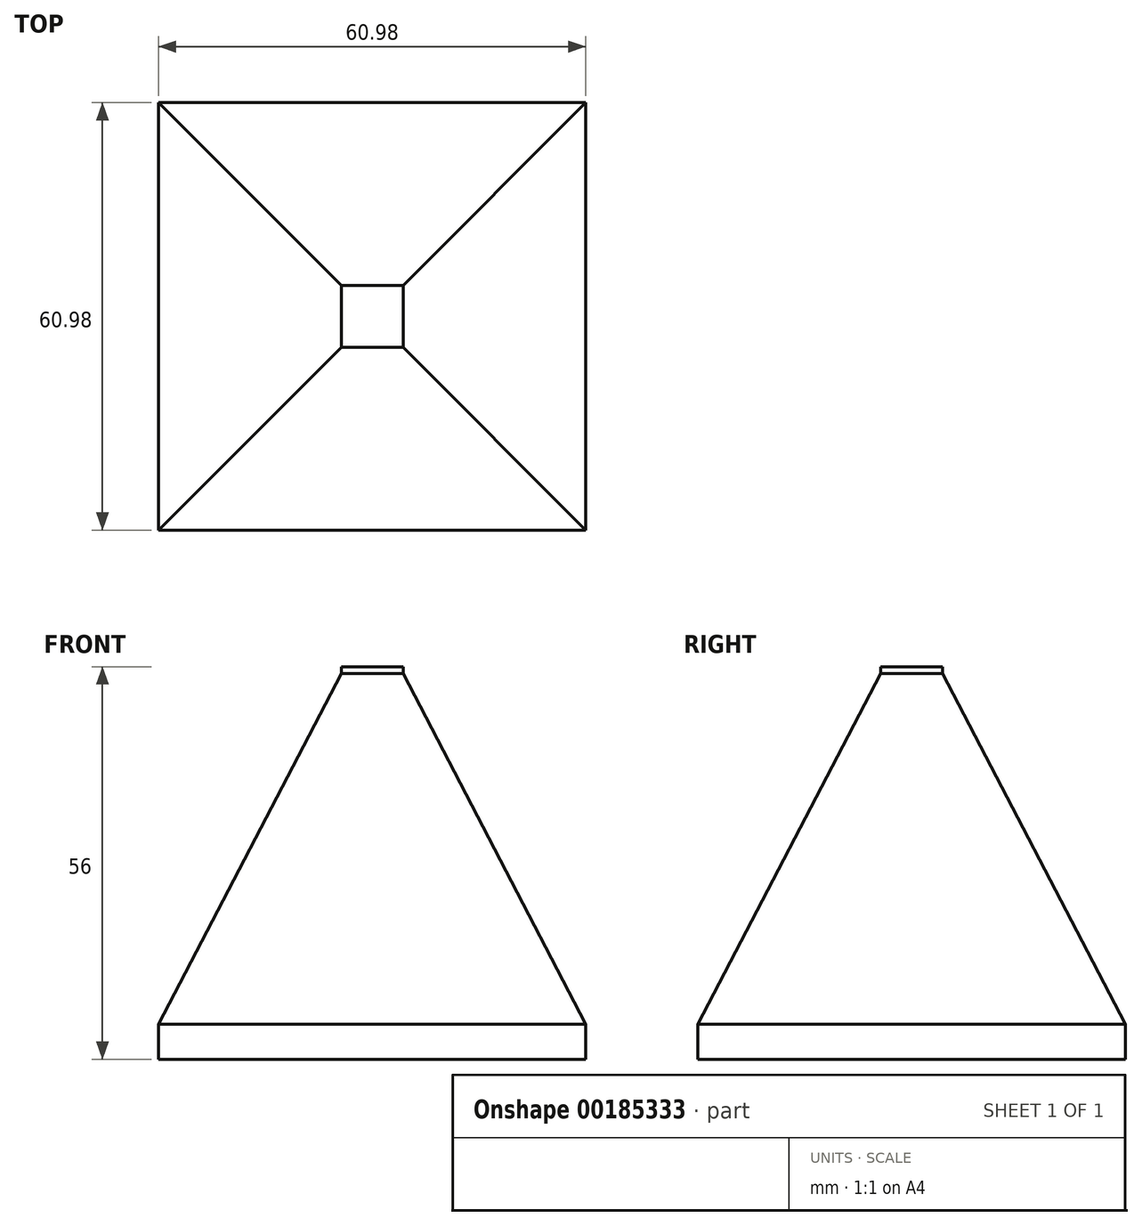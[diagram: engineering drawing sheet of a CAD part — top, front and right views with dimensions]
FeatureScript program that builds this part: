
annotation { "Feature Type Name" : "Feature", "Feature Type Description" : "" }
export const myFeature = defineFeature(function(context is Context, id is Id, definition is map)
    precondition{}
    {
        {
            var Q0;
            Q0=qCreatedBy(makeId("Top.planeOp"),FACE);
            var sketch = newSketch(context, id + "F0", { "sketchPlane" : qUnion([Q0])});
            skLineSegment(sketch, "E0.bottom", {"start": v(30.5, 30.5) * mm, "end": v(-30.5, 30.5) * mm});
            skLineSegment(sketch, "E0.top", {"start": v(30.5, -30.5) * mm, "end": v(-30.5, -30.5) * mm});
            skLineSegment(sketch, "E0.left", {"start": v(30.5, 30.5) * mm, "end": v(30.5, -30.5) * mm});
            skLineSegment(sketch, "E0.right", {"start": v(-30.5, 30.5) * mm, "end": v(-30.5, -30.5) * mm});
            skPoint(sketch, "E0.middle", {"position": v(0, 0) * mm});
            skSolve(sketch);
        }
        {
            var Q0;
            Q0=makeQuery(id+"F0.imprint","IMPRINT",FACE,{"disambiguationData":[TD([[makeQuery(id+"F0.imprint","IMPRINT",EDGE,{"derivedFrom":sQuery(id+"F0.wireOp",EDGE,"E0.bottom")}),1.0]])]});
            extrude(context, id + "F1", {"entities" : qUnion([Q0]), "depth" : 5 * mm});
        }
        {
            var Q0;
            Q0=makeQuery(id+"F1.opExtrude","CAP_FACE",FACE,{"disambiguationData":[OSD([sQuery(id+"F0.wireOp",EDGE,"E0.bottom"),sQuery(id+"F0.wireOp",EDGE,"E0.top"),sQuery(id+"F0.wireOp",EDGE,"E0.left"),sQuery(id+"F0.wireOp",EDGE,"E0.right")])],"isStart":false});
            cPlane(context, id + "F2", {"entities" : qUnion([Q0]), "cplaneType" : CPlaneType.OFFSET, "offset" : 50 * mm, "width" : 150 * mm, "height" : 150 * mm});
        }
        {
            var Q0;
            Q0=qCreatedBy(id+"F2.planeOp",FACE);
            var sketch = newSketch(context, id + "F3", { "sketchPlane" : qUnion([Q0])});
            skLineSegment(sketch, "E1.bottom", {"start": v(4.42, 4.42) * mm, "end": v(-4.42, 4.42) * mm});
            skLineSegment(sketch, "E1.top", {"start": v(4.42, -4.42) * mm, "end": v(-4.42, -4.42) * mm});
            skLineSegment(sketch, "E1.left", {"start": v(4.42, 4.42) * mm, "end": v(4.42, -4.42) * mm});
            skLineSegment(sketch, "E1.right", {"start": v(-4.42, 4.42) * mm, "end": v(-4.42, -4.42) * mm});
            skPoint(sketch, "E1.middle", {"position": v(0, 0) * mm});
            skSolve(sketch);
        }
        {
            var Q0;
            Q0 = qSketchRegion(id + "F3", true);
            extrude(context, id + "F4", {"entities" : qUnion([Q0]), "depth" : 1 * mm});
        }
        {
            var Q2;
            Q2=makeQuery(id+"F1.opExtrude","CAP_FACE",FACE,{"disambiguationData":[OSD([sQuery(id+"F0.wireOp",EDGE,"E0.bottom"),sQuery(id+"F0.wireOp",EDGE,"E0.top"),sQuery(id+"F0.wireOp",EDGE,"E0.left"),sQuery(id+"F0.wireOp",EDGE,"E0.right")])],"isStart":false});
            var Q3;
            Q3=makeQuery(id+"F4.opExtrude","CAP_FACE",FACE,{"disambiguationData":[OSD([sQuery(id+"F3.wireOp",EDGE,"E1.bottom"),sQuery(id+"F3.wireOp",EDGE,"E1.top"),sQuery(id+"F3.wireOp",EDGE,"E1.left"),sQuery(id+"F3.wireOp",EDGE,"E1.right")])],"isStart":true});
            loft(context, id + "F5", {"operationType" : NewBodyOperationType.ADD, "sheetProfilesArray" : [{ "sheetProfileEntities" : qUnion([Q2]) }, { "sheetProfileEntities" : qUnion([Q3]) }]});
        }
    });
